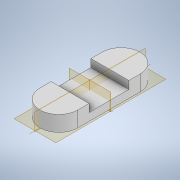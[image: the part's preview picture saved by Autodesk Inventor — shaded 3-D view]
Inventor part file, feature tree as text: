
AUTODESK INVENTOR PART (.ipt)
format: ipt  version: 2022.4 (Build 264492010, 492A)  size: 113,664 bytes
history: native  units: mm
features: extrude x2, sketch x1
ambient origin geometry x8: Origin, YZ Plane, XZ Plane, XY Plane, X Axis, Y Axis, Z Axis, Center Point
bodies: Solid1 (feature_tree)
feature tree (3):
  sketch  "Sketch1"  dims[d0=9.75mm d1=8.0mm d2=2.875mm d3=2.0mm d4=0.0mm d5=4.0mm d6=0.0mm]
  extrude  "Extrusion1"  Depth=8.0mm
  extrude  "Extrusion2"  Depth=4.0mm
